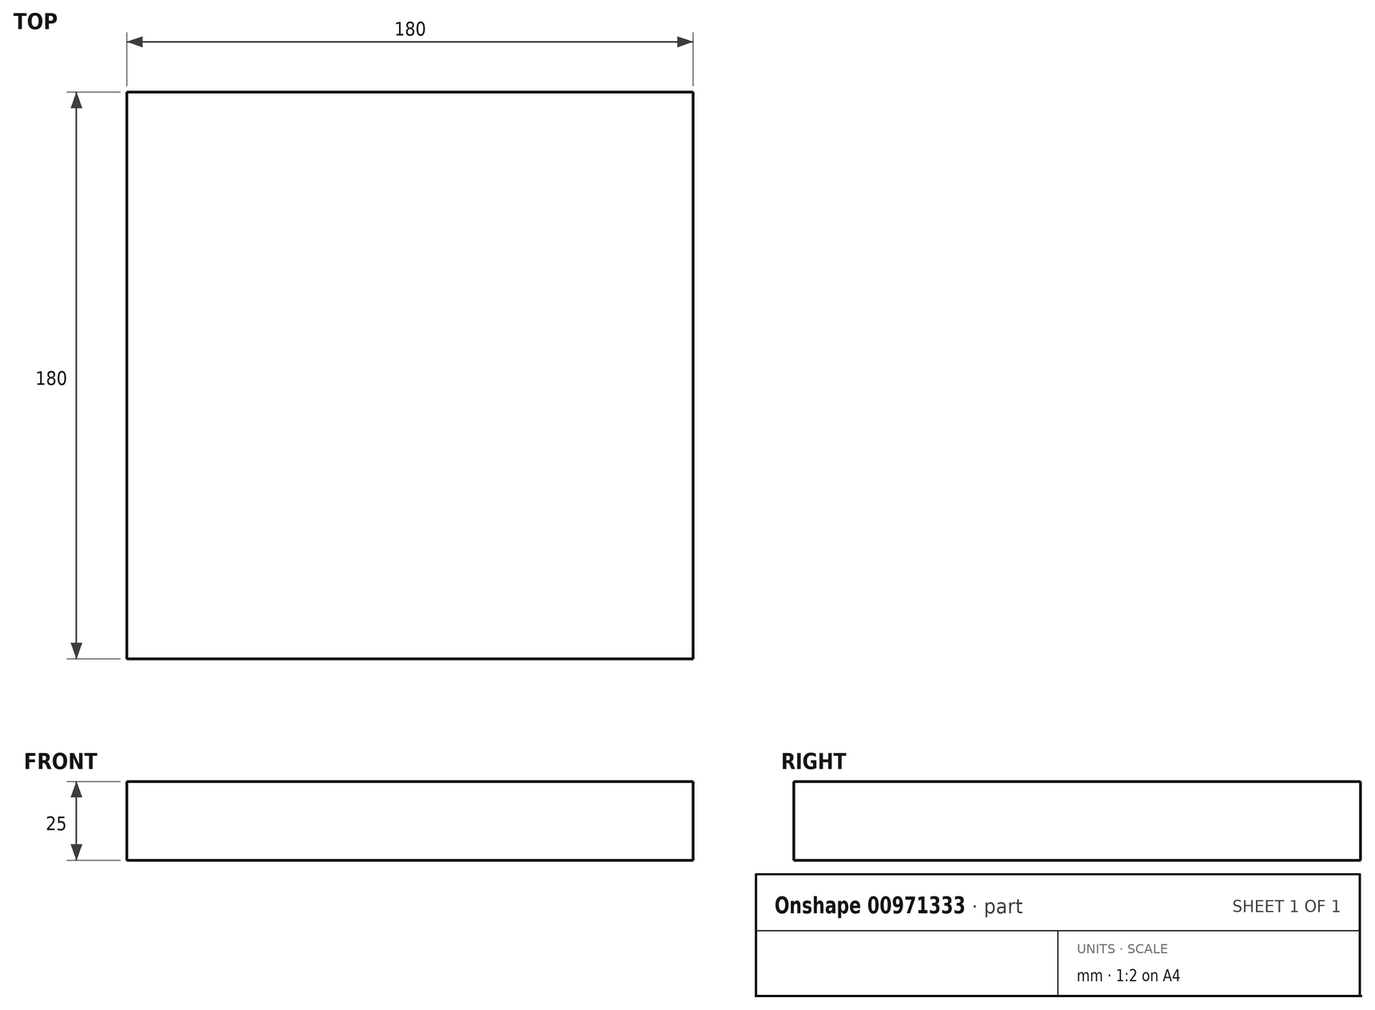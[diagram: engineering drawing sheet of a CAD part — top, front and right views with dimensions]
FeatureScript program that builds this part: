
annotation { "Feature Type Name" : "Feature", "Feature Type Description" : "" }
export const myFeature = defineFeature(function(context is Context, id is Id, definition is map)
    precondition{}
    {
        {
            var Q0;
            Q0=qCreatedBy(makeId("Top.planeOp"),FACE);
            var sketch = newSketch(context, id + "F0", { "sketchPlane" : qUnion([Q0])});
            skLineSegment(sketch, "E0.bottom", {"start": v(-79.55, 106.85) * mm, "end": v(100.45, 106.85) * mm});
            skLineSegment(sketch, "E0.top", {"start": v(-79.55, -73.15) * mm, "end": v(100.45, -73.15) * mm});
            skLineSegment(sketch, "E0.left", {"start": v(-79.55, 106.85) * mm, "end": v(-79.55, -73.15) * mm});
            skLineSegment(sketch, "E0.right", {"start": v(100.45, 106.85) * mm, "end": v(100.45, -73.15) * mm});
            skSolve(sketch);
        }
        {
            var Q0;
            Q0=makeQuery(id+"F0.imprint","IMPRINT",FACE,{"disambiguationData":[TD([[makeQuery(id+"F0.imprint","IMPRINT",EDGE,{"derivedFrom":sQuery(id+"F0.wireOp",EDGE,"E0.bottom")}),-1.0]])]});
            extrude(context, id + "F1", {"entities" : qUnion([Q0]), "depth" : 25 * mm, "offsetDistance" : 25 * mm});
        }
    });
